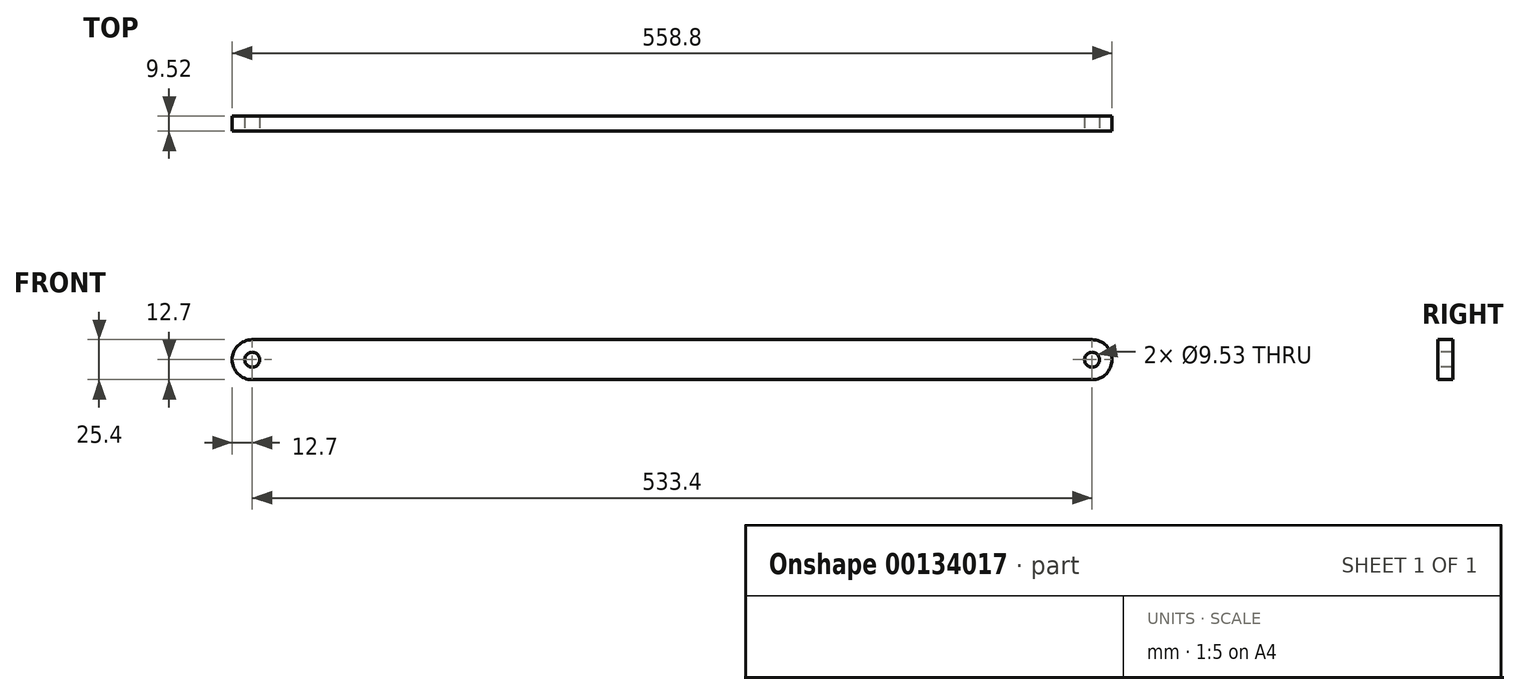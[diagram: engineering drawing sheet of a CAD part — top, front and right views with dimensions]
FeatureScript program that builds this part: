
annotation { "Feature Type Name" : "Feature", "Feature Type Description" : "" }
export const myFeature = defineFeature(function(context is Context, id is Id, definition is map)
    precondition{}
    {
        {
            var Q0;
            Q0=qCreatedBy(makeId("Front.planeOp"),FACE);
            var sketch = newSketch(context, id + "F0", { "sketchPlane" : qUnion([Q0])});
            skLineSegment(sketch, "E0", {"start": v(-266.7, 0) * mm, "end": v(266.7, 0) * mm, "construction": true});
            skLineSegment(sketch, "E1", {"start": v(-266.7, 12.7) * mm, "end": v(266.7, 12.7) * mm});
            skLineSegment(sketch, "E2", {"start": v(266.7, -12.7) * mm, "end": v(-266.7, -12.7) * mm});
            skArc(sketch, "E3", {"start": v(-266.7, -12.7) * mm, "mid": v(-279.4, 0) * mm, "end": v(-266.7, 12.7) * mm});
            skArc(sketch, "E4", {"start": v(266.7, 12.7) * mm, "mid": v(279.4, 0) * mm, "end": v(266.7, -12.7) * mm});
            skSolve(sketch);
        }
        {
            var Q0;
            Q0 = qSketchRegion(id + "F0", true);
            extrude(context, id + "F1", {"entities" : qUnion([Q0]), "endBound" : BoundingType.SYMMETRIC, "depth" : 9.52 * mm});
        }
        {
            var Q0;
            Q0=makeQuery(id+"F1.opExtrude","CAP_FACE",FACE,{"disambiguationData":[OSD([sQuery(id+"F0.wireOp",EDGE,"E1"),sQuery(id+"F0.wireOp",EDGE,"E2"),sQuery(id+"F0.wireOp",EDGE,"E3"),sQuery(id+"F0.wireOp",EDGE,"E4")])],"isStart":false});
            var sketch = newSketch(context, id + "F2", { "sketchPlane" : qUnion([Q0])});
            skPoint(sketch, "E5", {"position": v(-266.7, 0) * mm});
            skPoint(sketch, "E6", {"position": v(266.7, 0) * mm});
            skSolve(sketch);
        }
        {
            var Q0;
            Q0=sQuery(id+"F2.wireOp",VERTEX,"E5");
            var Q1;
            Q1=sQuery(id+"F2.wireOp",VERTEX,"E6");
            var Q2;
            Q2=makeQuery(id+"F1.opExtrude","SWEPT_BODY",BODY,{"disambiguationData":[OSD([sQuery(id+"F0.wireOp",EDGE,"E1"),sQuery(id+"F0.wireOp",EDGE,"E2"),sQuery(id+"F0.wireOp",EDGE,"E3"),sQuery(id+"F0.wireOp",EDGE,"E4")])]});
            hole(context, id + "F3", {"style" : HoleStyle.SIMPLE, "endStyle" : HoleEndStyle.THROUGH, "holeDiameter" : 9.52 * mm, "locations" : qUnion([Q0, Q1]), "scope" : qUnion([Q2]), "isTappedThrough" : true});
        }
    });
